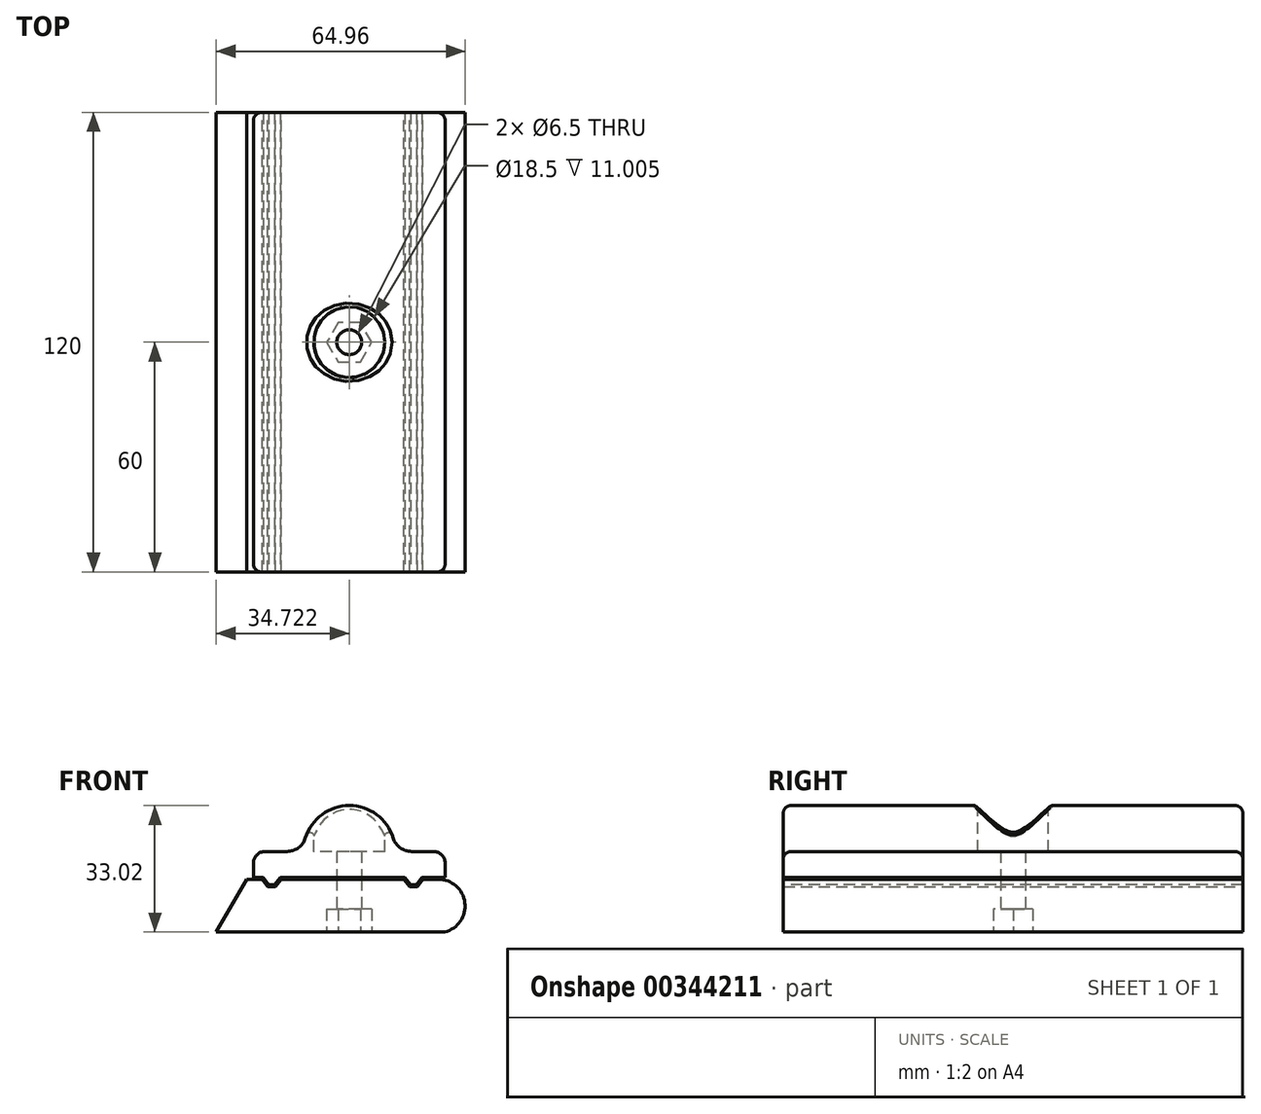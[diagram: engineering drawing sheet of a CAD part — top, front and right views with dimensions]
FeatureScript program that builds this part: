
annotation { "Feature Type Name" : "Feature", "Feature Type Description" : "" }
export const myFeature = defineFeature(function(context is Context, id is Id, definition is map)
    precondition{}
    {
        {
            var Q0;
            Q0=qCreatedBy(makeId("Front.planeOp"),FACE);
            var sketch = newSketch(context, id + "F0", { "sketchPlane" : qUnion([Q0])});
            skLineSegment(sketch, "E0.bottom", {"start": v(30.7, -6.9) * mm, "end": v(-28.98, -6.9) * mm});
            skLineSegment(sketch, "E0.top", {"start": v(28.98, 6.9) * mm, "end": v(24.98, 6.9) * mm});
            skPoint(sketch, "E0.middle", {"position": v(0, 0) * mm});
            skArc(sketch, "E1", {"start": v(30.7, -6.9) * mm, "mid": v(35.92, 0.76) * mm, "end": v(28.98, 6.9) * mm});
            skLineSegment(sketch, "E2", {"start": v(-28.98, -6.9) * mm, "end": v(-21.02, 6.9) * mm});
            skPoint(sketch, "E0.right.end.orphan", {"position": v(-30.7, 6.9) * mm});
            skLineSegment(sketch, "E3", {"start": v(30.7, -6.9) * mm, "end": v(30.7, -6.9) * mm});
            skLineSegment(sketch, "E4", {"start": v(-17.02, 6.9) * mm, "end": v(-15.52, 4.9) * mm});
            skLineSegment(sketch, "E5", {"start": v(-15.52, 4.9) * mm, "end": v(-13.52, 4.9) * mm});
            skLineSegment(sketch, "E6", {"start": v(-13.52, 4.9) * mm, "end": v(-12.02, 6.9) * mm});
            skLineSegment(sketch, "E7.trimOffspring", {"start": v(-17.02, 6.9) * mm, "end": v(-21.02, 6.9) * mm});
            skLineSegment(sketch, "E8", {"start": v(3.98, 6.9) * mm, "end": v(3.98, -0.97) * mm, "construction": true});
            skLineSegment(sketch, "E9.MirrorCS", {"start": v(21.48, 4.9) * mm, "end": v(19.98, 6.9) * mm});
            skLineSegment(sketch, "E10.MirrorCS", {"start": v(23.48, 4.9) * mm, "end": v(21.48, 4.9) * mm});
            skLineSegment(sketch, "E11.MirrorCS", {"start": v(24.98, 6.9) * mm, "end": v(23.48, 4.9) * mm});
            skLineSegment(sketch, "E12.trimOffspring", {"start": v(19.98, 6.9) * mm, "end": v(-12.02, 6.9) * mm});
            skSolve(sketch);
        }
        {
            var Q0;
            Q0 = qSketchRegion(id + "F0", true);
            extrude(context, id + "F1", {"entities" : qUnion([Q0]), "endBound" : BoundingType.SYMMETRIC, "depth" : 120 * mm});
        }
        {
            var Q0;
            Q0=makeQuery(id+"F1.opExtrude","CAP_FACE",FACE,{"disambiguationData":[OSD([sQuery(id+"F0.wireOp",EDGE,"E0.bottom"),sQuery(id+"F0.wireOp",EDGE,"E0.top"),sQuery(id+"F0.wireOp",EDGE,"E1"),sQuery(id+"F0.wireOp",EDGE,"E2"),sQuery(id+"F0.wireOp",EDGE,"E3"),sQuery(id+"F0.wireOp",EDGE,"E4"),sQuery(id+"F0.wireOp",EDGE,"E5"),sQuery(id+"F0.wireOp",EDGE,"E6"),sQuery(id+"F0.wireOp",EDGE,"E7.trimOffspring"),sQuery(id+"F0.wireOp",EDGE,"E9.MirrorCS"),sQuery(id+"F0.wireOp",EDGE,"E10.MirrorCS"),sQuery(id+"F0.wireOp",EDGE,"E11.MirrorCS"),sQuery(id+"F0.wireOp",EDGE,"E12.trimOffspring")])],"isStart":false});
            var sketch = newSketch(context, id + "F2", { "sketchPlane" : qUnion([Q0])});
            skLineSegment(sketch, "E13.0", {"start": v(-16.77, 7.4) * mm, "end": v(-19.26, 7.4) * mm});
            skLineSegment(sketch, "E13.1", {"start": v(-16.77, 7.4) * mm, "end": v(-15.27, 5.4) * mm});
            skLineSegment(sketch, "E13.2", {"start": v(-15.27, 5.4) * mm, "end": v(-13.77, 5.4) * mm});
            skLineSegment(sketch, "E13.3", {"start": v(-13.77, 5.4) * mm, "end": v(-12.27, 7.4) * mm});
            skLineSegment(sketch, "E13.4", {"start": v(20.23, 7.4) * mm, "end": v(-12.27, 7.4) * mm});
            skLineSegment(sketch, "E13.5", {"start": v(30.74, 7.4) * mm, "end": v(24.73, 7.4) * mm});
            skLineSegment(sketch, "E13.6", {"start": v(24.73, 7.4) * mm, "end": v(23.23, 5.4) * mm});
            skLineSegment(sketch, "E13.7", {"start": v(23.23, 5.4) * mm, "end": v(21.73, 5.4) * mm});
            skLineSegment(sketch, "E13.8", {"start": v(21.73, 5.4) * mm, "end": v(20.23, 7.4) * mm});
            skLineSegment(sketch, "E14", {"start": v(-19.26, 7.4) * mm, "end": v(-19.26, 14.13) * mm});
            skLineSegment(sketch, "E15", {"start": v(-19.26, 14.13) * mm, "end": v(-6.26, 14.13) * mm});
            skLineSegment(sketch, "E16", {"start": v(30.74, 14.13) * mm, "end": v(30.74, 7.4) * mm});
            skArc(sketch, "E17", {"start": v(17.74, 14.13) * mm, "mid": v(5.74, 26.13) * mm, "end": v(-6.26, 14.13) * mm});
            skLineSegment(sketch, "E18.trimOffspring", {"start": v(17.74, 14.13) * mm, "end": v(30.74, 14.13) * mm});
            skSolve(sketch);
        }
        {
            var Q0;
            Q0 = qSketchRegion(id + "F2", true);
            extrude(context, id + "F3", {"entities" : qUnion([Q0]), "oppositeDirection" : true, "depth" : 120 * mm});
        }
        {
            var Q0;
            Q0=makeQuery(id+"F3.opExtrude","SWEPT_EDGE",EDGE,{"disambiguationData":[OSD([sQuery(id+"F2.wireOp",EDGE,"E17"),sQuery(id+"F2.wireOp",EDGE,"E18.trimOffspring")])]});
            var Q1;
            Q1=makeQuery(id+"F3.opExtrude","SWEPT_EDGE",EDGE,{"disambiguationData":[OSD([sQuery(id+"F2.wireOp",EDGE,"E15"),sQuery(id+"F2.wireOp",EDGE,"E17")])]});
            fillet(context, id + "F4", {"entities" : qUnion([Q0, Q1]), "radius" : 5 * mm, "tangentPropagation" : true, "allowEdgeOverflow" : false});
        }
        {
            var Q0;
            Q0=makeQuery(id+"F3.opExtrude","SWEPT_EDGE",EDGE,{"disambiguationData":[OSD([sQuery(id+"F2.wireOp",EDGE,"E14"),sQuery(id+"F2.wireOp",EDGE,"E15")])]});
            var Q1;
            Q1=makeQuery(id+"F3.opExtrude","SWEPT_EDGE",EDGE,{"disambiguationData":[OSD([sQuery(id+"F2.wireOp",EDGE,"E16"),sQuery(id+"F2.wireOp",EDGE,"E18.trimOffspring")])]});
            fillet(context, id + "F5", {"entities" : qUnion([Q0, Q1]), "radius" : 3 * mm, "tangentPropagation" : true, "allowEdgeOverflow" : false});
        }
        {
            var Q0;
            Q0=qCreatedBy(makeId("Top.planeOp"),FACE);
            var sketch = newSketch(context, id + "F6", { "sketchPlane" : qUnion([Q0])});
            skLineSegment(sketch, "E19", {"start": v(5.74, -58.85) * mm, "end": v(5.74, -28.87) * mm});
            skLineSegment(sketch, "E20", {"start": v(5.74, 57.95) * mm, "end": v(5.74, -28.87) * mm});
            skLineSegment(sketch, "E21", {"start": v(5.74, 57.95) * mm, "end": v(5.74, 58.7) * mm});
            skCircle(sketch, "E22", {"center": v(5.74, 0) * mm, "radius": 3.25 * mm});
            skSolve(sketch);
        }
        {
            var Q0;
            Q0 = qSketchRegion(id + "F6", true);
            extrude(context, id + "F7", {"entities" : qUnion([Q0]), "operationType" : NewBodyOperationType.REMOVE, "endBound" : BoundingType.SYMMETRIC, "depth" : 68 * mm});
        }
        {
            var Q0;
            Q0=makeQuery(id+"F1.opExtrude","SWEPT_FACE",FACE,{"disambiguationData":[OSD([sQuery(id+"F0.wireOp",EDGE,"E0.bottom"),sQuery(id+"F0.wireOp",EDGE,"E3")])]});
            var sketch = newSketch(context, id + "F8", { "sketchPlane" : qUnion([Q0])});
            skCircle(sketch, "E23.cCircle", {"center": v(5.74, 0) * mm, "radius": 5.1 * mm, "construction": true});
            skLineSegment(sketch, "E23.0", {"start": v(-0.15, 0) * mm, "end": v(2.8, 5.1) * mm});
            skLineSegment(sketch, "E23.1", {"start": v(2.8, 5.1) * mm, "end": v(8.69, 5.1) * mm});
            skLineSegment(sketch, "E23.2", {"start": v(8.69, 5.1) * mm, "end": v(11.63, 0) * mm});
            skLineSegment(sketch, "E23.3", {"start": v(11.63, 0) * mm, "end": v(8.69, -5.1) * mm});
            skLineSegment(sketch, "E23.4", {"start": v(8.69, -5.1) * mm, "end": v(2.8, -5.1) * mm});
            skLineSegment(sketch, "E23.5", {"start": v(2.8, -5.1) * mm, "end": v(-0.15, 0) * mm});
            skPoint(sketch, "E23.0.midPoint", {"position": v(1.32, 2.55) * mm});
            skSolve(sketch);
        }
        {
            var Q0;
            Q0 = qSketchRegion(id + "F8", true);
            extrude(context, id + "F9", {"entities" : qUnion([Q0]), "operationType" : NewBodyOperationType.REMOVE, "oppositeDirection" : true, "depth" : 6 * mm});
        }
        {
            var Q0;
            Q0=sQuery(id+"F2.wireOp",EDGE,"E17");
            cPoint(context, id + "F10", {"entities" : qUnion([Q0]), "parameter" : 0.5});
        }
        {
            var Q0;
            Q0=qCreatedBy(makeId("Top.planeOp"),FACE);
            var Q1;
            Q1 = qCreatedBy(id + "F10" ,VERTEX);
            cPlane(context, id + "F11", {"entities" : qUnion([Q0, Q1]), "cplaneType" : CPlaneType.PLANE_POINT, "offset" : 29.2 * mm, "width" : 150 * mm, "height" : 150 * mm});
        }
        {
            var Q0;
            Q0=qCreatedBy(id+"F11.planeOp",FACE);
            var sketch = newSketch(context, id + "F12", { "sketchPlane" : qUnion([Q0])});
            skCircle(sketch, "E24.0", {"center": v(5.74, 0) * mm, "radius": 9.25 * mm});
            skSolve(sketch);
        }
        {
            var Q0;
            Q0 = qSketchRegion(id + "F12", true);
            extrude(context, id + "F13", {"entities" : qUnion([Q0]), "operationType" : NewBodyOperationType.REMOVE, "oppositeDirection" : true, "depth" : 12 * mm});
        }
        {
            var Q0;
            Q0=makeQuery(id+"F13.boolean.opBoolean","INTERSECT",EDGE,{"derivedFrom":[makeQuery(id+"F3.opExtrude","SWEPT_FACE",FACE,{"disambiguationData":[OSD([sQuery(id+"F2.wireOp",EDGE,"E17")])]}),makeQuery(id+"F13.opExtrude","SWEPT_FACE",FACE,{"disambiguationData":[OSD([sQuery(id+"F12.wireOp",EDGE,"E24.0")])]})]});
            fillet(context, id + "F14", {"entities" : qUnion([Q0]), "radius" : 1 * mm, "tangentPropagation" : true, "allowEdgeOverflow" : false});
        }
        {
            var Q0;
            Q0=makeQuery(id+"F3.opExtrude","CAP_EDGE",EDGE,{"disambiguationData":[OSD([sQuery(id+"F2.wireOp",EDGE,"E17")])],"isStart":true});
            var Q1;
            Q1=makeQuery(id+"F3.opExtrude","CAP_EDGE",EDGE,{"disambiguationData":[OSD([sQuery(id+"F2.wireOp",EDGE,"E17")])],"isStart":false});
            fillet(context, id + "F15", {"entities" : qUnion([Q0, Q1]), "radius" : 2 * mm, "tangentPropagation" : true, "allowEdgeOverflow" : false});
        }
    });
